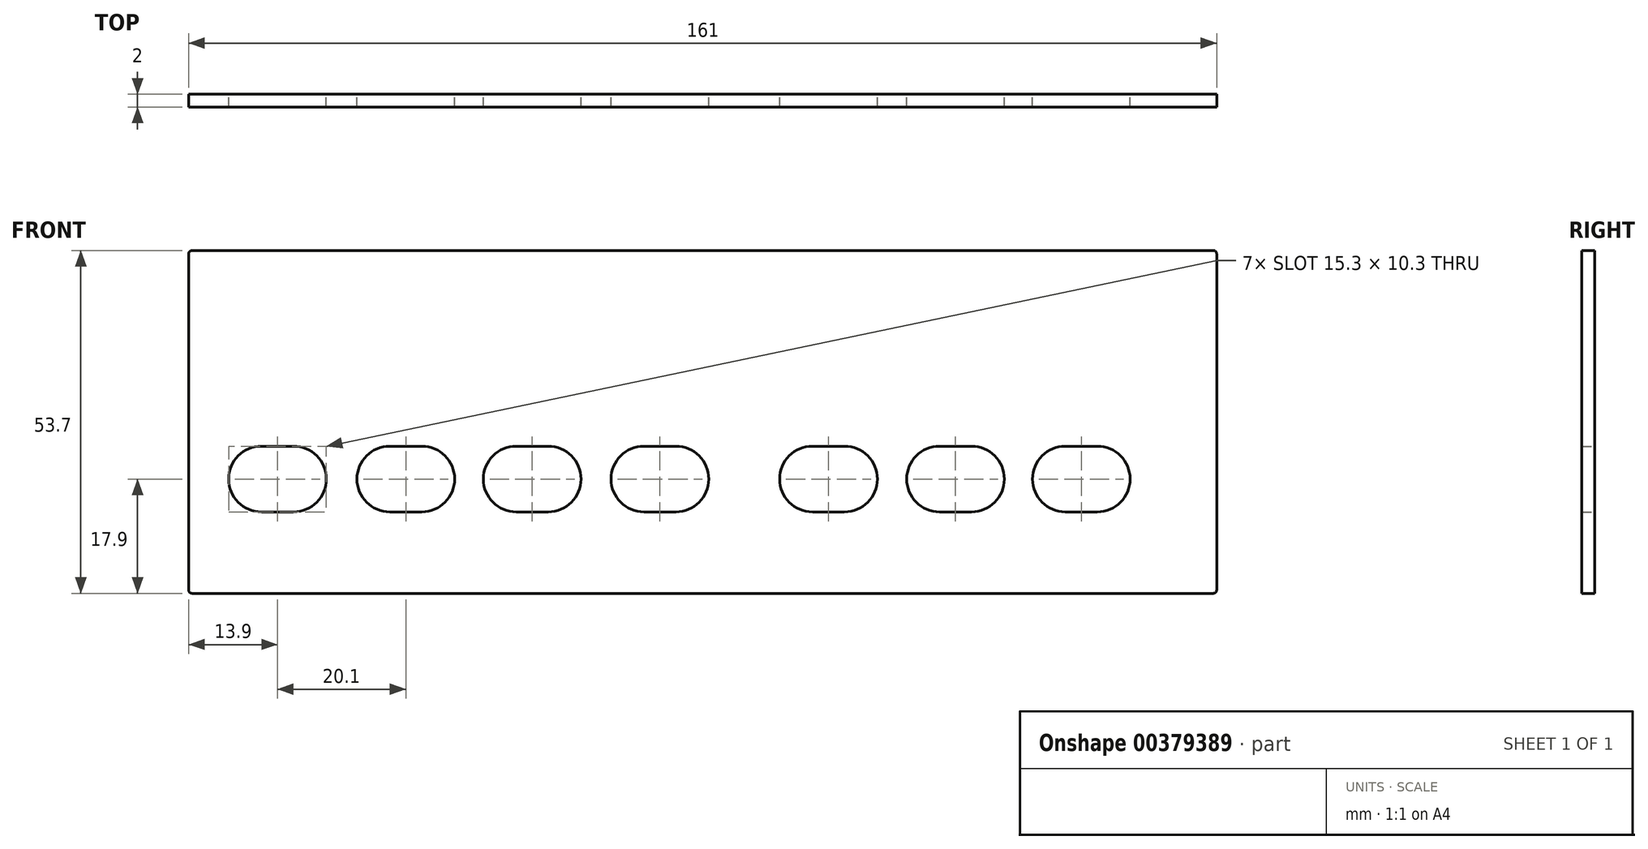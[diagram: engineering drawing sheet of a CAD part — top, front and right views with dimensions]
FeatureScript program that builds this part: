
annotation { "Feature Type Name" : "Feature", "Feature Type Description" : "" }
export const myFeature = defineFeature(function(context is Context, id is Id, definition is map)
    precondition{}
    {
        {
            var Q0;
            Q0=qCreatedBy(makeId("Front.planeOp"),FACE);
            var sketch = newSketch(context, id + "F0", { "sketchPlane" : qUnion([Q0])});
            skLineSegment(sketch, "E0.bottom", {"start": v(80, 26.85) * mm, "end": v(-80, 26.85) * mm});
            skLineSegment(sketch, "E0.top", {"start": v(80, -26.85) * mm, "end": v(-80, -26.85) * mm});
            skLineSegment(sketch, "E0.left", {"start": v(80.5, 26.35) * mm, "end": v(80.5, -26.35) * mm});
            skLineSegment(sketch, "E0.right", {"start": v(-80.5, 26.35) * mm, "end": v(-80.5, -26.35) * mm});
            skPoint(sketch, "E0.middle", {"position": v(0, 0) * mm});
            skPoint(sketch, "E1.visualSharp", {"position": v(-80.5, 26.85) * mm});
            skArc(sketch, "E1.filletArc", {"start": v(-80, 26.85) * mm, "mid": v(-80.35, 26.7) * mm, "end": v(-80.5, 26.35) * mm});
            skPoint(sketch, "E2.visualSharp", {"position": v(-80.5, -26.85) * mm});
            skArc(sketch, "E2.filletArc", {"start": v(-80.5, -26.35) * mm, "mid": v(-80.35, -26.7) * mm, "end": v(-80, -26.85) * mm});
            skPoint(sketch, "E3.visualSharp", {"position": v(80.5, -26.85) * mm});
            skArc(sketch, "E3.filletArc", {"start": v(80, -26.85) * mm, "mid": v(80.35, -26.7) * mm, "end": v(80.5, -26.35) * mm});
            skPoint(sketch, "E4.visualSharp", {"position": v(80.5, 26.85) * mm});
            skArc(sketch, "E4.filletArc", {"start": v(80.5, 26.35) * mm, "mid": v(80.35, 26.7) * mm, "end": v(80, 26.85) * mm});
            skLineSegment(sketch, "E5.bottom", {"start": v(-69.1, -3.8) * mm, "end": v(-64.1, -3.8) * mm});
            skLineSegment(sketch, "E5.top", {"start": v(-69.1, -14.1) * mm, "end": v(-64.1, -14.1) * mm});
            skLineSegment(sketch, "E5.left", {"start": v(-74.25, -8.95) * mm, "end": v(-74.25, -8.95) * mm});
            skLineSegment(sketch, "E5.right", {"start": v(-58.95, -8.95) * mm, "end": v(-58.95, -8.95) * mm});
            skPoint(sketch, "E6.visualSharp", {"position": v(-74.25, -3.8) * mm});
            skArc(sketch, "E6.filletArc", {"start": v(-69.1, -3.8) * mm, "mid": v(-72.74, -5.3) * mm, "end": v(-74.25, -8.95) * mm});
            skPoint(sketch, "E7.visualSharp", {"position": v(-74.25, -14.1) * mm});
            skArc(sketch, "E7.filletArc", {"start": v(-74.25, -8.95) * mm, "mid": v(-72.74, -12.6) * mm, "end": v(-69.1, -14.1) * mm});
            skPoint(sketch, "E8.visualSharp", {"position": v(-58.95, -14.1) * mm});
            skArc(sketch, "E8.filletArc", {"start": v(-64.1, -14.1) * mm, "mid": v(-60.46, -12.6) * mm, "end": v(-58.95, -8.95) * mm});
            skPoint(sketch, "E9.visualSharp", {"position": v(-58.95, -3.8) * mm});
            skArc(sketch, "E9.filletArc", {"start": v(-58.95, -8.95) * mm, "mid": v(-60.46, -5.3) * mm, "end": v(-64.1, -3.8) * mm});
            skLineSegment(sketch, "E10.bottom", {"start": v(-49, -3.8) * mm, "end": v(-44, -3.8) * mm});
            skLineSegment(sketch, "E10.top", {"start": v(-49, -14.1) * mm, "end": v(-44, -14.1) * mm});
            skLineSegment(sketch, "E10.left", {"start": v(-54.15, -8.95) * mm, "end": v(-54.15, -8.95) * mm});
            skLineSegment(sketch, "E10.right", {"start": v(-38.85, -8.95) * mm, "end": v(-38.85, -8.95) * mm});
            skPoint(sketch, "E11.visualSharp", {"position": v(-54.15, -3.8) * mm});
            skArc(sketch, "E11.filletArc", {"start": v(-49, -3.8) * mm, "mid": v(-52.64, -5.3) * mm, "end": v(-54.15, -8.95) * mm});
            skPoint(sketch, "E12.visualSharp", {"position": v(-54.15, -14.1) * mm});
            skArc(sketch, "E12.filletArc", {"start": v(-54.15, -8.95) * mm, "mid": v(-52.64, -12.6) * mm, "end": v(-49, -14.1) * mm});
            skPoint(sketch, "E13.visualSharp", {"position": v(-38.85, -14.1) * mm});
            skArc(sketch, "E13.filletArc", {"start": v(-44, -14.1) * mm, "mid": v(-40.36, -12.6) * mm, "end": v(-38.85, -8.95) * mm});
            skPoint(sketch, "E14.visualSharp", {"position": v(-38.85, -3.8) * mm});
            skArc(sketch, "E14.filletArc", {"start": v(-38.85, -8.95) * mm, "mid": v(-40.36, -5.3) * mm, "end": v(-44, -3.8) * mm});
            skLineSegment(sketch, "E15.bottom", {"start": v(-29.2, -3.8) * mm, "end": v(-24.2, -3.8) * mm});
            skLineSegment(sketch, "E15.top", {"start": v(-29.2, -14.1) * mm, "end": v(-24.2, -14.1) * mm});
            skLineSegment(sketch, "E15.left", {"start": v(-34.35, -8.95) * mm, "end": v(-34.35, -8.95) * mm});
            skLineSegment(sketch, "E15.right", {"start": v(-19.05, -8.95) * mm, "end": v(-19.05, -8.95) * mm});
            skPoint(sketch, "E16.visualSharp", {"position": v(-34.35, -3.8) * mm});
            skArc(sketch, "E16.filletArc", {"start": v(-29.2, -3.8) * mm, "mid": v(-32.84, -5.3) * mm, "end": v(-34.35, -8.95) * mm});
            skPoint(sketch, "E17.visualSharp", {"position": v(-34.35, -14.1) * mm});
            skArc(sketch, "E17.filletArc", {"start": v(-34.35, -8.95) * mm, "mid": v(-32.84, -12.6) * mm, "end": v(-29.2, -14.1) * mm});
            skPoint(sketch, "E18.visualSharp", {"position": v(-19.05, -14.1) * mm});
            skArc(sketch, "E18.filletArc", {"start": v(-24.2, -14.1) * mm, "mid": v(-20.56, -12.6) * mm, "end": v(-19.05, -8.95) * mm});
            skPoint(sketch, "E19.visualSharp", {"position": v(-19.05, -3.8) * mm});
            skArc(sketch, "E19.filletArc", {"start": v(-19.05, -8.95) * mm, "mid": v(-20.56, -5.3) * mm, "end": v(-24.2, -3.8) * mm});
            skLineSegment(sketch, "E20.bottom", {"start": v(-9.2, -3.8) * mm, "end": v(-4.2, -3.8) * mm});
            skLineSegment(sketch, "E20.top", {"start": v(-9.2, -14.1) * mm, "end": v(-4.2, -14.1) * mm});
            skLineSegment(sketch, "E20.left", {"start": v(-14.35, -8.95) * mm, "end": v(-14.35, -8.95) * mm});
            skLineSegment(sketch, "E20.right", {"start": v(0.95, -8.95) * mm, "end": v(0.95, -8.95) * mm});
            skPoint(sketch, "E21.visualSharp", {"position": v(-14.35, -3.8) * mm});
            skArc(sketch, "E21.filletArc", {"start": v(-9.2, -3.8) * mm, "mid": v(-12.84, -5.3) * mm, "end": v(-14.35, -8.95) * mm});
            skPoint(sketch, "E22.visualSharp", {"position": v(-14.35, -14.1) * mm});
            skArc(sketch, "E22.filletArc", {"start": v(-14.35, -8.95) * mm, "mid": v(-12.84, -12.6) * mm, "end": v(-9.2, -14.1) * mm});
            skPoint(sketch, "E23.visualSharp", {"position": v(0.95, -14.1) * mm});
            skArc(sketch, "E23.filletArc", {"start": v(-4.2, -14.1) * mm, "mid": v(-0.56, -12.6) * mm, "end": v(0.95, -8.95) * mm});
            skPoint(sketch, "E24.visualSharp", {"position": v(0.95, -3.8) * mm});
            skArc(sketch, "E24.filletArc", {"start": v(0.95, -8.95) * mm, "mid": v(-0.56, -5.3) * mm, "end": v(-4.2, -3.8) * mm});
            skLineSegment(sketch, "E25.bottom", {"start": v(17.2, -3.8) * mm, "end": v(22.2, -3.8) * mm});
            skLineSegment(sketch, "E25.top", {"start": v(17.2, -14.1) * mm, "end": v(22.2, -14.1) * mm});
            skLineSegment(sketch, "E25.left", {"start": v(12.05, -8.95) * mm, "end": v(12.05, -8.95) * mm});
            skLineSegment(sketch, "E25.right", {"start": v(27.35, -8.95) * mm, "end": v(27.35, -8.95) * mm});
            skPoint(sketch, "E26.visualSharp", {"position": v(12.05, -3.8) * mm});
            skArc(sketch, "E26.filletArc", {"start": v(17.2, -3.8) * mm, "mid": v(13.56, -5.3) * mm, "end": v(12.05, -8.95) * mm});
            skPoint(sketch, "E27.visualSharp", {"position": v(12.05, -14.1) * mm});
            skArc(sketch, "E27.filletArc", {"start": v(12.05, -8.95) * mm, "mid": v(13.56, -12.6) * mm, "end": v(17.2, -14.1) * mm});
            skPoint(sketch, "E28.visualSharp", {"position": v(27.35, -14.1) * mm});
            skArc(sketch, "E28.filletArc", {"start": v(22.2, -14.1) * mm, "mid": v(25.84, -12.6) * mm, "end": v(27.35, -8.95) * mm});
            skPoint(sketch, "E29.visualSharp", {"position": v(27.35, -3.8) * mm});
            skArc(sketch, "E29.filletArc", {"start": v(27.35, -8.95) * mm, "mid": v(25.84, -5.3) * mm, "end": v(22.2, -3.8) * mm});
            skLineSegment(sketch, "E30.bottom", {"start": v(37.1, -3.8) * mm, "end": v(42.1, -3.8) * mm});
            skLineSegment(sketch, "E30.top", {"start": v(37.1, -14.1) * mm, "end": v(42.1, -14.1) * mm});
            skLineSegment(sketch, "E30.left", {"start": v(31.95, -8.95) * mm, "end": v(31.95, -8.95) * mm});
            skLineSegment(sketch, "E30.right", {"start": v(47.25, -8.95) * mm, "end": v(47.25, -8.95) * mm});
            skPoint(sketch, "E31.visualSharp", {"position": v(31.95, -3.8) * mm});
            skArc(sketch, "E31.filletArc", {"start": v(37.1, -3.8) * mm, "mid": v(33.46, -5.3) * mm, "end": v(31.95, -8.95) * mm});
            skPoint(sketch, "E32.visualSharp", {"position": v(31.95, -14.1) * mm});
            skArc(sketch, "E32.filletArc", {"start": v(31.95, -8.95) * mm, "mid": v(33.46, -12.6) * mm, "end": v(37.1, -14.1) * mm});
            skPoint(sketch, "E33.visualSharp", {"position": v(47.25, -14.1) * mm});
            skArc(sketch, "E33.filletArc", {"start": v(42.1, -14.1) * mm, "mid": v(45.74, -12.6) * mm, "end": v(47.25, -8.95) * mm});
            skPoint(sketch, "E34.visualSharp", {"position": v(47.25, -3.8) * mm});
            skArc(sketch, "E34.filletArc", {"start": v(47.25, -8.95) * mm, "mid": v(45.74, -5.3) * mm, "end": v(42.1, -3.8) * mm});
            skLineSegment(sketch, "E35.bottom", {"start": v(56.8, -3.8) * mm, "end": v(61.8, -3.8) * mm});
            skLineSegment(sketch, "E35.top", {"start": v(56.8, -14.1) * mm, "end": v(61.8, -14.1) * mm});
            skLineSegment(sketch, "E35.left", {"start": v(51.65, -8.95) * mm, "end": v(51.65, -8.95) * mm});
            skLineSegment(sketch, "E35.right", {"start": v(66.95, -8.95) * mm, "end": v(66.95, -8.95) * mm});
            skPoint(sketch, "E36.visualSharp", {"position": v(51.65, -3.8) * mm});
            skArc(sketch, "E36.filletArc", {"start": v(56.8, -3.8) * mm, "mid": v(53.16, -5.3) * mm, "end": v(51.65, -8.95) * mm});
            skPoint(sketch, "E37.visualSharp", {"position": v(51.65, -14.1) * mm});
            skArc(sketch, "E37.filletArc", {"start": v(51.65, -8.95) * mm, "mid": v(53.16, -12.6) * mm, "end": v(56.8, -14.1) * mm});
            skPoint(sketch, "E38.visualSharp", {"position": v(66.95, -14.1) * mm});
            skArc(sketch, "E38.filletArc", {"start": v(61.8, -14.1) * mm, "mid": v(65.44, -12.6) * mm, "end": v(66.95, -8.95) * mm});
            skPoint(sketch, "E39.visualSharp", {"position": v(66.95, -3.8) * mm});
            skArc(sketch, "E39.filletArc", {"start": v(66.95, -8.95) * mm, "mid": v(65.44, -5.3) * mm, "end": v(61.8, -3.8) * mm});
            skSolve(sketch);
        }
        {
            var Q0;
            Q0=makeQuery(id+"F0.imprint","IMPRINT",FACE,{"disambiguationData":[TD([[makeQuery(id+"F0.imprint","IMPRINT",EDGE,{"derivedFrom":sQuery(id+"F0.wireOp",EDGE,"E0.bottom")}),1.0]])]});
            extrude(context, id + "F1", {"entities" : qUnion([Q0]), "depth" : 2 * mm});
        }
    });
